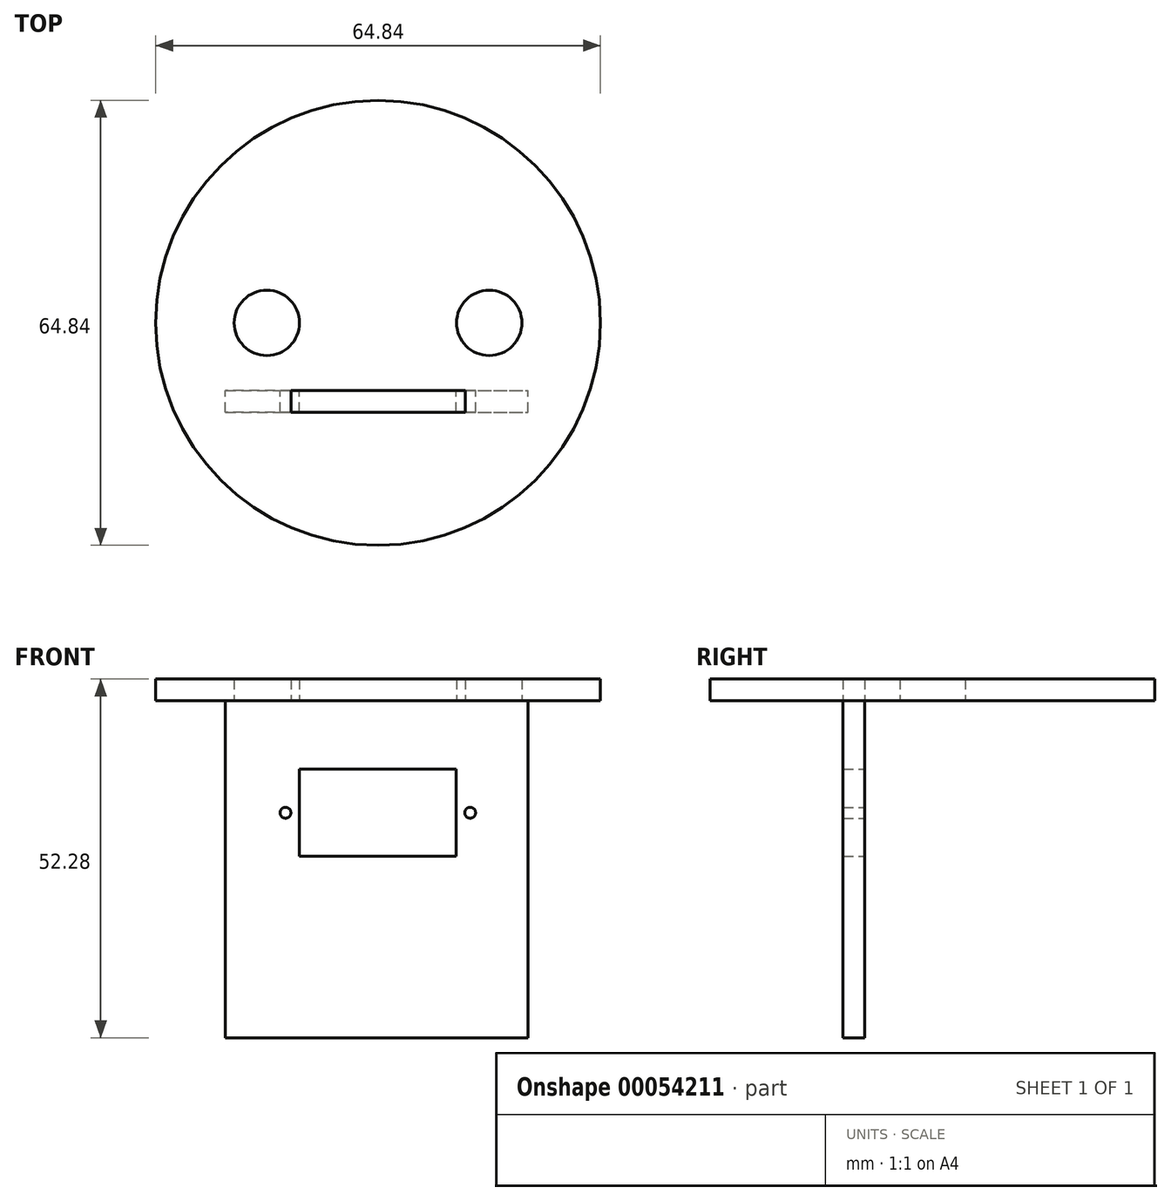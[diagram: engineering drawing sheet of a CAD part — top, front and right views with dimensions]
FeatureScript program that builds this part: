
annotation { "Feature Type Name" : "Feature", "Feature Type Description" : "" }
export const myFeature = defineFeature(function(context is Context, id is Id, definition is map)
    precondition{}
    {
        {
            var Q0;
            Q0=qCreatedBy(makeId("Top.planeOp"),FACE);
            var sketch = newSketch(context, id + "F0", { "sketchPlane" : qUnion([Q0])});
            skCircle(sketch, "E0", {"center": v(0, 0) * mm, "radius": 32.42 * mm});
            skLineSegment(sketch, "E1", {"start": v(0, 0) * mm, "end": v(81.07, 0) * mm, "construction": true});
            skCircle(sketch, "E2", {"center": v(16.21, 0) * mm, "radius": 4.76 * mm});
            skCircle(sketch, "E3", {"center": v(-16.21, 0) * mm, "radius": 4.76 * mm});
            skLineSegment(sketch, "E4.bottom", {"start": v(-12.7, -9.88) * mm, "end": v(12.7, -9.88) * mm});
            skLineSegment(sketch, "E4.top", {"start": v(-12.7, -13.05) * mm, "end": v(12.7, -13.05) * mm});
            skLineSegment(sketch, "E4.left", {"start": v(-12.7, -9.88) * mm, "end": v(-12.7, -13.05) * mm});
            skLineSegment(sketch, "E4.right", {"start": v(12.7, -9.88) * mm, "end": v(12.7, -13.05) * mm});
            skLineSegment(sketch, "E5", {"start": v(0, 0) * mm, "end": v(0, -9.88) * mm, "construction": true});
            skSolve(sketch);
        }
        {
            var Q0;
            Q0=makeQuery(id+"F0.imprint","IMPRINT",FACE,{"disambiguationData":[TD([[makeQuery(id+"F0.imprint","IMPRINT",EDGE,{"derivedFrom":sQuery(id+"F0.wireOp",EDGE,"E0")}),1.0]])]});
            extrude(context, id + "F1", {"entities" : qUnion([Q0]), "depth" : 3.17 * mm});
        }
        {
            var Q0;
            Q0=makeQuery(id+"F1.opExtrude","SWEPT_FACE",FACE,{"disambiguationData":[OSD([sQuery(id+"F0.wireOp",EDGE,"E4.bottom")])]});
            var sketch = newSketch(context, id + "F2", { "sketchPlane" : qUnion([Q0])});
            skLineSegment(sketch, "E6", {"start": v(-12.7, 3.18) * mm, "end": v(12.7, 3.18) * mm});
            skLineSegment(sketch, "E7", {"start": v(12.7, 3.18) * mm, "end": v(12.7, 0) * mm});
            skLineSegment(sketch, "E8", {"start": v(12.7, 0) * mm, "end": v(21.85, 0) * mm});
            skLineSegment(sketch, "E9", {"start": v(-12.7, 3.18) * mm, "end": v(-12.7, 0) * mm});
            skLineSegment(sketch, "E10", {"start": v(-12.7, 0) * mm, "end": v(-22.24, 0) * mm});
            skLineSegment(sketch, "E11", {"start": v(-22.24, 0) * mm, "end": v(-22.24, -49.1) * mm});
            skLineSegment(sketch, "E12", {"start": v(-22.24, -49.1) * mm, "end": v(21.85, -49.1) * mm});
            skLineSegment(sketch, "E13", {"start": v(21.85, -49.1) * mm, "end": v(21.85, 0) * mm});
            skLineSegment(sketch, "E14.bottom", {"start": v(-11.46, -9.96) * mm, "end": v(11.4, -9.96) * mm});
            skLineSegment(sketch, "E14.top", {"start": v(-11.46, -22.66) * mm, "end": v(11.4, -22.66) * mm});
            skLineSegment(sketch, "E14.left", {"start": v(-11.46, -9.96) * mm, "end": v(-11.46, -22.66) * mm});
            skLineSegment(sketch, "E14.right", {"start": v(11.4, -9.96) * mm, "end": v(11.4, -22.66) * mm});
            skPoint(sketch, "E15", {"position": v(-0.03, -9.96) * mm});
            skCircle(sketch, "E16", {"center": v(13.43, -16.31) * mm, "radius": 0.8 * mm});
            skPoint(sketch, "E16.centerSnap0", {"position": v(11.4, -16.31) * mm});
            skCircle(sketch, "E17", {"center": v(-13.5, -16.31) * mm, "radius": 0.8 * mm});
            skPoint(sketch, "E17.centerSnap0", {"position": v(-11.46, -16.31) * mm});
            skSolve(sketch);
        }
        {
            var Q0;
            Q0=makeQuery(id+"F2.imprint","IMPRINT",FACE,{"disambiguationData":[TD([[makeQuery(id+"F2.imprint","IMPRINT",EDGE,{"derivedFrom":sQuery(id+"F2.wireOp",EDGE,"E8")}),-1.0]])]});
            var Q1;
            Q1=makeQuery(id+"F2.imprint","IMPRINT",FACE,{"disambiguationData":[TD([[makeQuery(id+"F2.imprint","IMPRINT",EDGE,{"derivedFrom":sQuery(id+"F2.wireOp",EDGE,"E6")}),-1.0]])]});
            extrude(context, id + "F3", {"entities" : qUnion([Q0, Q1]), "depth" : 3.17 * mm});
        }
    });
